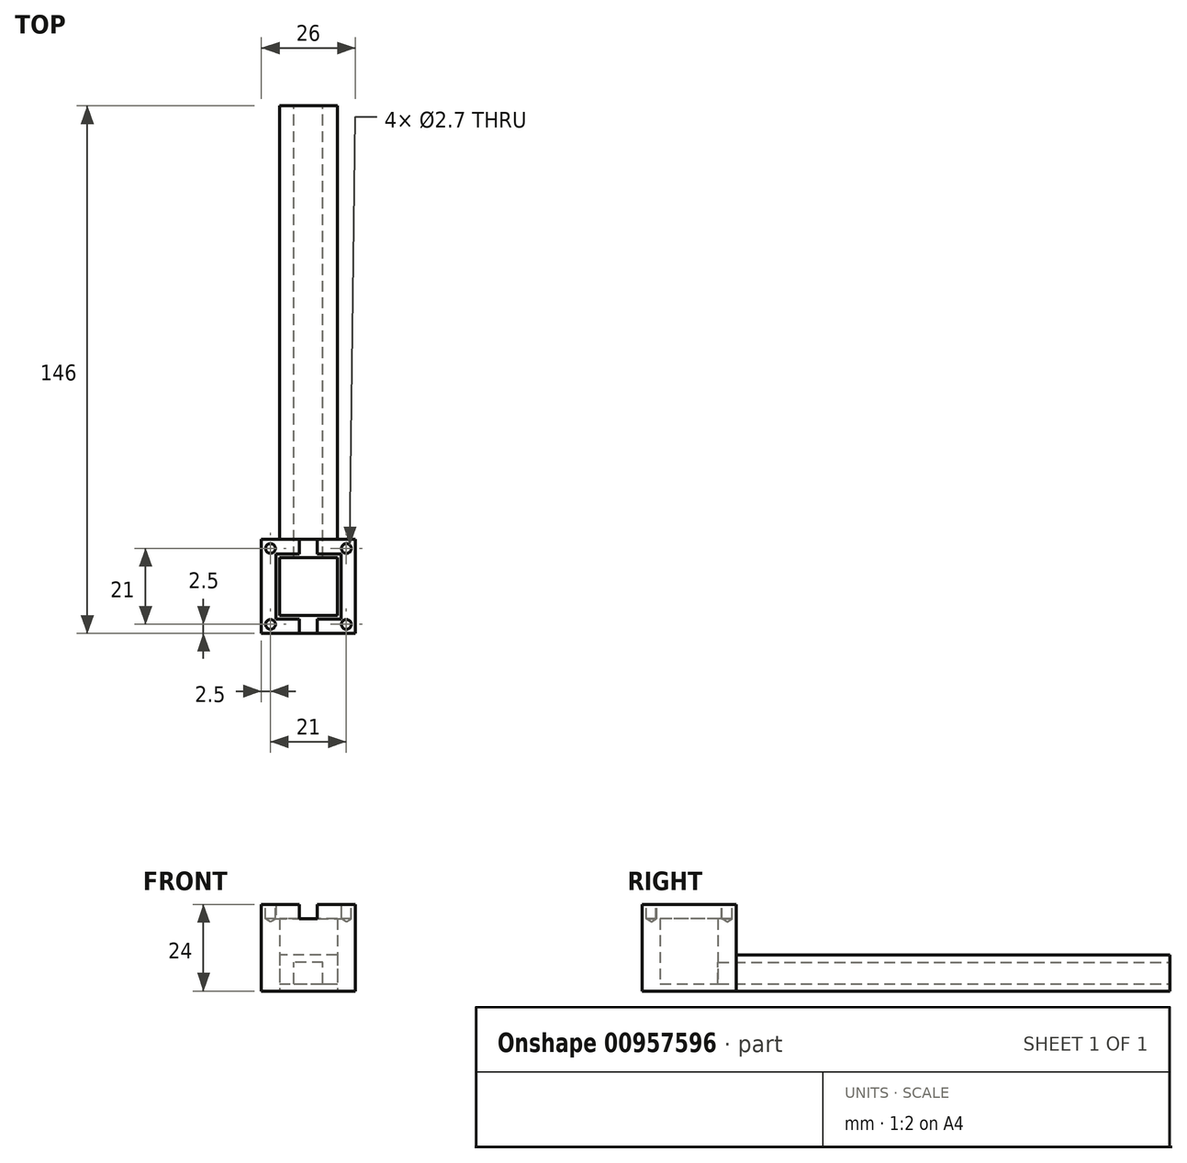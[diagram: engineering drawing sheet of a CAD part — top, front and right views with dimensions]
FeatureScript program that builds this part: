
annotation { "Feature Type Name" : "Feature", "Feature Type Description" : "" }
export const myFeature = defineFeature(function(context is Context, id is Id, definition is map)
    precondition{}
    {
        {
            var Q0;
            Q0=qCreatedBy(makeId("Top.planeOp"),FACE);
            var sketch = newSketch(context, id + "F0", { "sketchPlane" : qUnion([Q0])});
            skLineSegment(sketch, "E0.bottom", {"start": v(13, 13) * mm, "end": v(-13, 13) * mm});
            skLineSegment(sketch, "E0.top", {"start": v(13, -13) * mm, "end": v(-13, -13) * mm});
            skLineSegment(sketch, "E0.left", {"start": v(13, 13) * mm, "end": v(13, -13) * mm});
            skLineSegment(sketch, "E0.right", {"start": v(-13, 13) * mm, "end": v(-13, -13) * mm});
            skPoint(sketch, "E0.middle", {"position": v(0, 0) * mm});
            skLineSegment(sketch, "E1.bottom", {"start": v(8, 8) * mm, "end": v(-8, 8) * mm});
            skLineSegment(sketch, "E1.top", {"start": v(8, -8) * mm, "end": v(-8, -8) * mm});
            skLineSegment(sketch, "E1.left", {"start": v(8, 8) * mm, "end": v(8, -8) * mm});
            skLineSegment(sketch, "E1.right", {"start": v(-8, 8) * mm, "end": v(-8, -8) * mm});
            skSolve(sketch);
        }
        {
            var Q0;
            Q0=makeQuery(id+"F0.imprint","IMPRINT",FACE,{"disambiguationData":[TD([[makeQuery(id+"F0.imprint","IMPRINT",EDGE,{"derivedFrom":sQuery(id+"F0.wireOp",EDGE,"E0.bottom")}),1.0]])]});
            var Q1;
            Q1=makeQuery(id+"F0.imprint","IMPRINT",FACE,{"disambiguationData":[TD([[makeQuery(id+"F0.imprint","IMPRINT",EDGE,{"derivedFrom":sQuery(id+"F0.wireOp",EDGE,"E1.bottom")}),-1.0]])]});
            var Q2;
            Q2=makeQuery(id+"F0.imprint","IMPRINT",FACE,{"disambiguationData":[TD([[makeQuery(id+"F0.imprint","IMPRINT",EDGE,{"derivedFrom":sQuery(id+"F0.wireOp",EDGE,"E1.bottom")}),1.0]])]});
            extrude(context, id + "F1", {"entities" : qUnion([Q0, Q1, Q2]), "depth" : 2 * mm, "offsetDistance" : 25 * mm});
        }
        {
            var Q0;
            Q0=qSketchRegion(id+"F0",true);
            var Q1;
            Q1=makeQuery(id+"F0.imprint","IMPRINT",FACE,{"disambiguationData":[TD([[makeQuery(id+"F0.imprint","IMPRINT",EDGE,{"derivedFrom":sQuery(id+"F0.wireOp",EDGE,"E1.bottom")}),-1.0]])]});
            extrude(context, id + "F2", {"entities" : qUnion([Q0, Q1]), "operationType" : NewBodyOperationType.ADD, "depth" : 20 * mm, "offsetDistance" : 25 * mm});
        }
        {
            var Q0;
            Q0=makeQuery(id+"F2.opExtrude","CAP_FACE",FACE,{"disambiguationData":[OSD([sQuery(id+"F0.wireOp",EDGE,"E0.bottom"),sQuery(id+"F0.wireOp",EDGE,"E0.top"),sQuery(id+"F0.wireOp",EDGE,"E0.left"),sQuery(id+"F0.wireOp",EDGE,"E0.right"),sQuery(id+"F0.wireOp",EDGE,"E1.bottom"),sQuery(id+"F0.wireOp",EDGE,"E1.top"),sQuery(id+"F0.wireOp",EDGE,"E1.left"),sQuery(id+"F0.wireOp",EDGE,"E1.right")])],"isStart":false});
            var sketch = newSketch(context, id + "F3", { "sketchPlane" : qUnion([Q0])});
            skLineSegment(sketch, "E2.bottom", {"start": v(-9, 9) * mm, "end": v(9, 9) * mm});
            skLineSegment(sketch, "E2.top", {"start": v(-9, -9) * mm, "end": v(9, -9) * mm});
            skLineSegment(sketch, "E2.left", {"start": v(-9, 9) * mm, "end": v(-9, -9) * mm});
            skLineSegment(sketch, "E2.right", {"start": v(9, 9) * mm, "end": v(9, -9) * mm});
            skPoint(sketch, "E2.middle", {"position": v(0, 0) * mm});
            skSolve(sketch);
        }
        {
            var Q0;
            Q0=makeQuery(id+"F3.imprint","IMPRINT",FACE,{"disambiguationData":[TD([[makeQuery(id+"F3.imprint","IMPRINT",EDGE,{"derivedFrom":sQuery(id+"F3.wireOp",EDGE,"E2.bottom")}),1.0]])]});
            extrude(context, id + "F4", {"entities" : qUnion([Q0]), "operationType" : NewBodyOperationType.ADD, "depth" : 4 * mm, "offsetDistance" : 25 * mm});
        }
        {
            var Q0;
            Q0=makeQuery(id+"F4.opExtrude","CAP_FACE",FACE,{"disambiguationData":[OSD([sQuery(id+"F0.wireOp",EDGE,"E0.bottom"),sQuery(id+"F0.wireOp",EDGE,"E0.top"),sQuery(id+"F0.wireOp",EDGE,"E0.left"),sQuery(id+"F0.wireOp",EDGE,"E0.right"),sQuery(id+"F3.wireOp",EDGE,"E2.bottom"),sQuery(id+"F3.wireOp",EDGE,"E2.top"),sQuery(id+"F3.wireOp",EDGE,"E2.left"),sQuery(id+"F3.wireOp",EDGE,"E2.right")])],"isStart":false});
            var sketch = newSketch(context, id + "F5", { "sketchPlane" : qUnion([Q0])});
            skLineSegment(sketch, "E3", {"start": v(-2.5, 13) * mm, "end": v(-2.5, 9) * mm});
            skLineSegment(sketch, "E4.MirrorCS", {"start": v(2.5, 13) * mm, "end": v(2.5, 9) * mm});
            skLineSegment(sketch, "E5.MirrorCS", {"start": v(2.5, -13) * mm, "end": v(2.5, -9) * mm});
            skLineSegment(sketch, "E6.MirrorCS", {"start": v(-2.5, -13) * mm, "end": v(-2.5, -9) * mm});
            skLineSegment(sketch, "E7", {"start": v(-13, 13) * mm, "end": v(-9, 9) * mm, "construction": true});
            skPoint(sketch, "E8", {"position": v(-10.5, 10.5) * mm});
            skPoint(sketch, "E9.MirrorP", {"position": v(10.5, 10.5) * mm});
            skLineSegment(sketch, "E10.MirrorCS", {"start": v(13, 13) * mm, "end": v(9, 9) * mm, "construction": true});
            skLineSegment(sketch, "E11.MirrorCS", {"start": v(-13, -13) * mm, "end": v(-9, -9) * mm, "construction": true});
            skPoint(sketch, "E12.MirrorP", {"position": v(-10.5, -10.5) * mm});
            skLineSegment(sketch, "E13.MirrorCS", {"start": v(13, -13) * mm, "end": v(9, -9) * mm, "construction": true});
            skPoint(sketch, "E14.MirrorP", {"position": v(10.5, -10.5) * mm});
            skSolve(sketch);
        }
        {
            var Q0;
            {var subQ0=sQuery(id+"F5.wireOp",EDGE,"E5.MirrorCS");Q0=makeQuery(id+"F5.imprint","IMPRINT",FACE,{"disambiguationData":[TD([[makeQuery(id+"F5.imprint","IMPRINT",EDGE,{"derivedFrom":subQ0}),1.0]])]});}
            var Q1;
            {var subQ0=sQuery(id+"F5.wireOp",EDGE,"E3");Q1=makeQuery(id+"F5.imprint","IMPRINT",FACE,{"disambiguationData":[TD([[makeQuery(id+"F5.imprint","IMPRINT",EDGE,{"derivedFrom":subQ0}),1.0]])]});}
            var Q2;
            Q2=makeQuery(id+"F2.opExtrude","CAP_FACE",FACE,{"disambiguationData":[OSD([sQuery(id+"F0.wireOp",EDGE,"E0.bottom"),sQuery(id+"F0.wireOp",EDGE,"E0.top"),sQuery(id+"F0.wireOp",EDGE,"E0.left"),sQuery(id+"F0.wireOp",EDGE,"E0.right"),sQuery(id+"F0.wireOp",EDGE,"E1.bottom"),sQuery(id+"F0.wireOp",EDGE,"E1.top"),sQuery(id+"F0.wireOp",EDGE,"E1.left"),sQuery(id+"F0.wireOp",EDGE,"E1.right")])],"isStart":false});
            extrude(context, id + "F6", {"entities" : qUnion([Q0, Q1]), "operationType" : NewBodyOperationType.REMOVE, "endBound" : BoundingType.UP_TO_SURFACE, "oppositeDirection" : true, "depth" : 25 * mm, "endBoundEntityFace" : qUnion([Q2]), "offsetDistance" : 25 * mm});
        }
        {
            var Q0;
            Q0=sQuery(id+"F5.wireOp",VERTEX,"E8");
            var Q1;
            Q1=sQuery(id+"F5.wireOp",VERTEX,"E9.MirrorP");
            var Q2;
            Q2=sQuery(id+"F5.wireOp",VERTEX,"E12.MirrorP");
            var Q3;
            Q3=sQuery(id+"F5.wireOp",VERTEX,"E14.MirrorP");
            var Q4;
            Q4=makeQuery(id+"F1.opExtrude","SWEPT_BODY",BODY,{"disambiguationData":[OSD([sQuery(id+"F0.wireOp",EDGE,"E0.bottom"),sQuery(id+"F0.wireOp",EDGE,"E0.top"),sQuery(id+"F0.wireOp",EDGE,"E0.left"),sQuery(id+"F0.wireOp",EDGE,"E0.right")])]});
            hole(context, id + "F7", {"style" : HoleStyle.SIMPLE, "endStyle" : HoleEndStyle.BLIND, "standardTappedOrClearance" : lookupTablePath({ "standard" : "ISO", "engagement" : "50%", "pitch" : "0.5 mm", "size" : "M3", "type" : "Tapped" }), "standardBlindInLast" : lookupTablePath({ "standard" : "ISO", "fit" : "Normal", "engagement" : "50%", "pitch" : "0.5 mm", "size" : "M3", "type" : "Clearance & tapped" }), "holeDiameter" : 2.7 * mm, "majorDiameter" : 3 * mm, "showTappedDepth" : true, "holeDepth" : 4 * mm, "isTappedThrough" : true, "tappedDepth" : 2.5 * mm, "tapClearance" : 3, "locations" : qUnion([Q0, Q1, Q2, Q3]), "scope" : qUnion([Q4])});
        }
        {
            var Q0;
            {var subQ0=sQuery(id+"F0.wireOp",EDGE,"E0.left");Q0=makeQuery(id+"F4.boolean.opBoolean","MERGE",FACE,{"derivedFrom":[makeQuery(id+"F2.boolean.opBoolean","MERGE",FACE,{"derivedFrom":[makeQuery(id+"F1.opExtrude","SWEPT_FACE",FACE,{"disambiguationData":[OSD([subQ0])]}),makeQuery(id+"F2.opExtrude","SWEPT_FACE",FACE,{"disambiguationData":[OSD([subQ0])]})]}),makeQuery(id+"F4.opExtrude","SWEPT_FACE",FACE,{"disambiguationData":[OSD([subQ0])]})]});}
            var sketch = newSketch(context, id + "F8", { "sketchPlane" : qUnion([Q0])});
            skLineSegment(sketch, "E15.bottom", {"start": v(-7.98, 18) * mm, "end": v(8.02, 18) * mm});
            skLineSegment(sketch, "E15.top", {"start": v(-7.98, 2) * mm, "end": v(8.02, 2) * mm});
            skLineSegment(sketch, "E15.left", {"start": v(-7.98, 18) * mm, "end": v(-7.98, 2) * mm});
            skLineSegment(sketch, "E15.right", {"start": v(8.02, 18) * mm, "end": v(8.02, 2) * mm});
            skLineSegment(sketch, "E16", {"start": v(-7.98, 0) * mm, "end": v(-7.98, 20) * mm, "construction": true});
            skLineSegment(sketch, "E17", {"start": v(8.02, 0) * mm, "end": v(8.02, 20) * mm, "construction": true});
            skSolve(sketch);
        }
        {
            var Q0;
            {var subQ0=sQuery(id+"F0.wireOp",EDGE,"E0.bottom");Q0=makeQuery(id+"F4.boolean.opBoolean","MERGE",FACE,{"derivedFrom":[makeQuery(id+"F2.boolean.opBoolean","MERGE",FACE,{"derivedFrom":[makeQuery(id+"F1.opExtrude","SWEPT_FACE",FACE,{"disambiguationData":[OSD([subQ0])]}),makeQuery(id+"F2.opExtrude","SWEPT_FACE",FACE,{"disambiguationData":[OSD([subQ0])]})]}),makeQuery(id+"F4.opExtrude","SWEPT_FACE",FACE,{"disambiguationData":[OSD([subQ0])]})]});}
            var sketch = newSketch(context, id + "F9", { "sketchPlane" : qUnion([Q0])});
            skLineSegment(sketch, "E18.bottom", {"start": v(-8, 10) * mm, "end": v(8, 10) * mm});
            skLineSegment(sketch, "E18.top", {"start": v(-8, 0) * mm, "end": v(8, 0) * mm});
            skLineSegment(sketch, "E18.left", {"start": v(-8, 10) * mm, "end": v(-8, 0) * mm});
            skLineSegment(sketch, "E18.right", {"start": v(8, 10) * mm, "end": v(8, 0) * mm});
            skLineSegment(sketch, "E19", {"start": v(-8, 0) * mm, "end": v(-8, 10) * mm, "construction": true});
            skLineSegment(sketch, "E20", {"start": v(8, 0) * mm, "end": v(8, 10) * mm, "construction": true});
            skLineSegment(sketch, "E21.bottom", {"start": v(4, 8) * mm, "end": v(-4, 8) * mm});
            skLineSegment(sketch, "E21.top", {"start": v(4, 2) * mm, "end": v(-4, 2) * mm});
            skLineSegment(sketch, "E21.left", {"start": v(4, 8) * mm, "end": v(4, 2) * mm});
            skLineSegment(sketch, "E21.right", {"start": v(-4, 8) * mm, "end": v(-4, 2) * mm});
            skSolve(sketch);
        }
        {
            var Q0;
            Q0=makeQuery(id+"F9.imprint","IMPRINT",FACE,{"disambiguationData":[TD([[makeQuery(id+"F9.imprint","IMPRINT",EDGE,{"derivedFrom":sQuery(id+"F9.wireOp",EDGE,"E21.bottom")}),1.0]])]});
            extrude(context, id + "F10", {"entities" : qUnion([Q0]), "operationType" : NewBodyOperationType.REMOVE, "oppositeDirection" : true, "depth" : 10.28 * mm, "offsetDistance" : 25 * mm});
        }
        {
            var Q0;
            Q0=makeQuery(id+"F9.imprint","IMPRINT",FACE,{"disambiguationData":[TD([[makeQuery(id+"F9.imprint","IMPRINT",EDGE,{"derivedFrom":sQuery(id+"F9.wireOp",EDGE,"E18.bottom")}),-1.0]])]});
            extrude(context, id + "F11", {"entities" : qUnion([Q0]), "operationType" : NewBodyOperationType.ADD, "depth" : 120 * mm, "offsetDistance" : 25 * mm});
        }
    });
